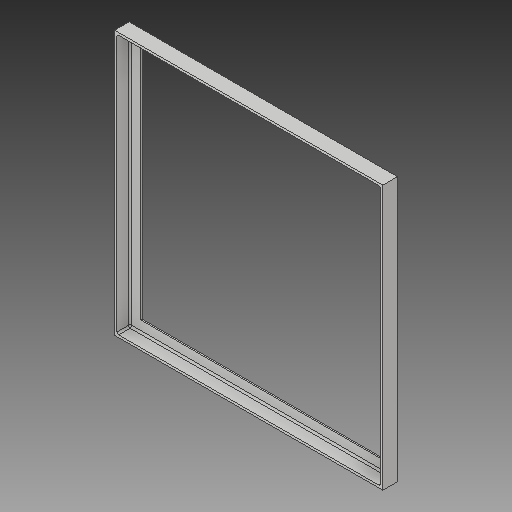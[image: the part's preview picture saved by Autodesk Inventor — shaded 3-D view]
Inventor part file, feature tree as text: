
AUTODESK INVENTOR PART (.ipt)
format: ipt  version: 2017 (Build 210142000, 142)  size: 124,416 bytes
history: native  units: in
note: dims shown in document units (in); Inventor stores cm internally (conversion verified against a paired STEP export)
features: extrude x2, sketch x2, fillet x1
ambient origin geometry x8: Origin, YZ Plane, XZ Plane, XY Plane, X Axis, Y Axis, Z Axis, Center Point
bodies: Solid1 (feature_tree)
feature tree (5):
  extrude  "Extrusion1"  Depth=20.0in
  extrude  "Extrusion2"  Depth=0.1046in TaperAngle=0.0deg
  fillet  "Fillet1"  Radius=1.0in
  sketch  "Sketch1"  dims[d0=20.3125in d1=20.0in]
  sketch  "Sketch2"  dims[d2=1.0in d3=0.1046in d4=0.0in d5=1.0in d6=0.0in d7=0.125in]
